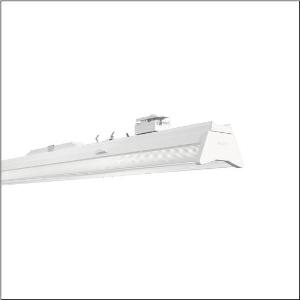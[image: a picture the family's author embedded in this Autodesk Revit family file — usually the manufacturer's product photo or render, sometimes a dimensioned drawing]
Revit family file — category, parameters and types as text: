
# Revit family: licross_21_performance_ho_52td16mn4e5m
name_source: partatom
category: Lighting Fixtures
units: mm (PartAtom-declared; Revit-internal decimal feet)

## family parameters
Cut with Voids When Loaded = No
Host = Face
Light Source = No
Part Type = Normal
Room Calculation Point = No
Round Connector Dimension = Use Diameter
Shared = No

## types (1)
- --- (1 x LED, 14970 lm, 83.2 W, 4000K)
    Apparent Load = 83 VA
    CIE Flux Codes = 63 87 95 78 100
    Color Rendering = 80
    Color Temperature = 4000K
    Default Elevation = 1800 mm
    Description = Licross 21 Performance HO, luminaire insert, of sheet steel, galvanised, coil coated, white, length: 1.500mm, width: 120mm, height: 123mm, LED rated luminous flux: 14.970lm, light colour: 840, SDCM (Standard Deviation of Colour Matching)MacAdam ≤ 3 SDCM (initial), control gear: ON/OFF Multilumen, with plug, 3-pole, with phase selection, mains connection: 220..240V, AC, 50/60Hz, rated input power: 83W, internal wiring halogen-free, primary light control with lens, of plastic, primary optical cover: cover, of PMMA, light emission: direct/indirect distribution, primary light characteristic: symmetric, protection rating (complete): IP54, insulation class (complete): insulation class I (protective earthing), certification: CE, ENEC, UKCA, protection symbol: D if used in an environment with non-conductive dust loads with corresponding accessories, impact resistance: IK06, permissible ambient temperature for indoor applications: -35..+35°C, corresponds to IFS (International Featured Standards) requirements for safety and quality in the food industry, reducing of maximum allowable ambient temperature of 5°C with ceiling mounting, LABS conformity tested according to VDMA 24364:2018-05, The light source and the operating device comply with the requirements of the Ecodesign Regulation (EU) 2019/2020 and are replaceable in accordance with this regulation, packaging unit: 1 piece
    Height = 114 mm
    Lamp = 1 x LED
    Lamp Light Flux = 14970 lm
    Lamp Power = 83.2 W
    Lamp count = 1
    Length = 1500 mm
    Luminous efficacy = 180 lm/W
    Manufacturer = Siteco
    ModVariant = No
    Model = 52TD16MN4E5M
    Mounting Place = Ceiling
    Mounting Type = Pendant
    Number of Poles = 1
    OnlyDefault = Yes
    Power Factor = 1
    Product Name = Licross 21 Performance HO
    Product group = luminaire insert | ceiling pendant
    ProductGroupID = 901
    Protection Class = Protection class I
    Protection Degree = IP 54
    RLX_Detail_Level = 1
    RLX_Emergency_Light_Flux = 0 lm
    RLX_Emergency_Type = 0
    RLX_Emergency_Type_DB = No
    RlxData = <blob elided: 32081 chars, md5=5ef9fd9d>
    Socket = socket
    Standby Power = 0 W
    System Light Flux = 14970 lm
    System Power = 83 W
    Type Comments = factory setting: luminous flux: 100 % | (A | C | E) | 195 mA
    Type Image = l_1256138.jpg
    URL = http://relux.com
    VarID = @adj_110741
    Voltage = 0 V
    Weight = 0.00 kg
    Width = 120 mm

## geometry (parser evidence)
native form markers: Blend x4, Sweep x11
no freeform markers — native parametric forms only
